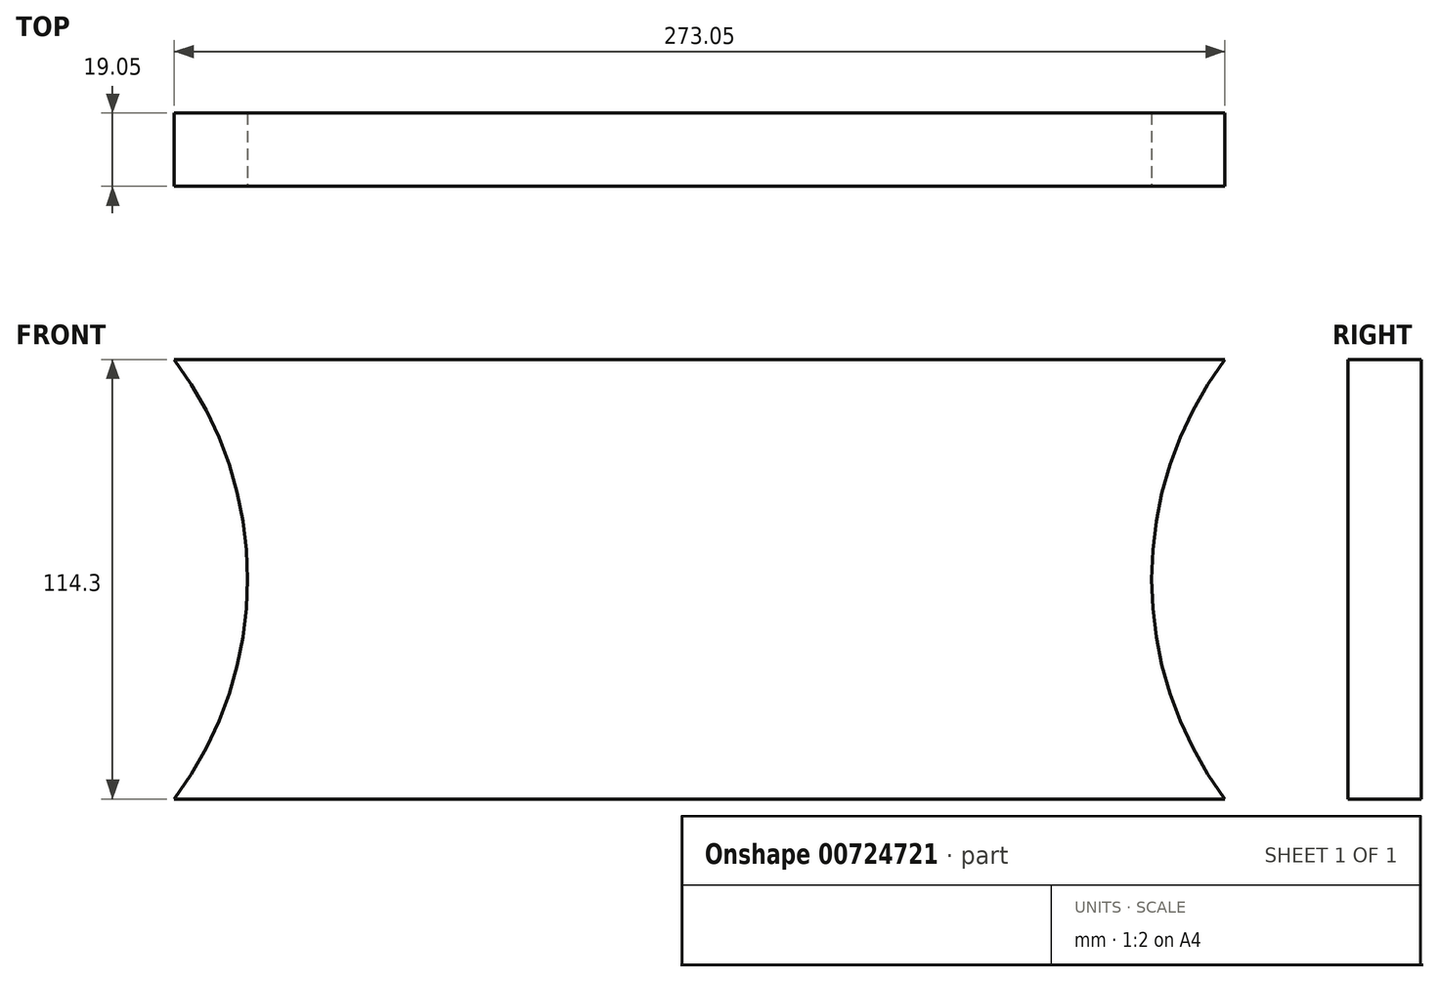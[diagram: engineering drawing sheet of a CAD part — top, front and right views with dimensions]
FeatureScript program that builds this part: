
annotation { "Feature Type Name" : "Feature", "Feature Type Description" : "" }
export const myFeature = defineFeature(function(context is Context, id is Id, definition is map)
    precondition{}
    {
        {
            var Q0;
            Q0=qCreatedBy(makeId("Front.planeOp"),FACE);
            var sketch = newSketch(context, id + "F0", { "sketchPlane" : qUnion([Q0])});
            skLineSegment(sketch, "E0.bottom", {"start": v(0, 0) * mm, "end": v(273.05, 0) * mm});
            skLineSegment(sketch, "E0.top", {"start": v(0, 114.3) * mm, "end": v(273.05, 114.3) * mm});
            skLineSegment(sketch, "E0.left", {"start": v(0, 0) * mm, "end": v(0, 114.3) * mm});
            skLineSegment(sketch, "E0.right", {"start": v(273.05, 0) * mm, "end": v(273.05, 114.3) * mm});
            skSolve(sketch);
        }
        {
            var Q0;
            Q0=qSketchRegion(id+"F0",true);
            extrude(context, id + "F1", {"entities" : qUnion([Q0]), "depth" : 19.05 * mm, "offsetDistance" : 25.4 * mm});
        }
        {
            var Q0;
            Q0=makeQuery(id+"F1.opExtrude","CAP_FACE",FACE,{"disambiguationData":[OSD([sQuery(id+"F0.wireOp",EDGE,"E0.bottom"),sQuery(id+"F0.wireOp",EDGE,"E0.top"),sQuery(id+"F0.wireOp",EDGE,"E0.left"),sQuery(id+"F0.wireOp",EDGE,"E0.right")])],"isStart":false});
            var sketch = newSketch(context, id + "F2", { "sketchPlane" : qUnion([Q0])});
            skArc(sketch, "E1", {"start": v(0, 0) * mm, "mid": v(19.05, 57.15) * mm, "end": v(0, 114.3) * mm});
            skArc(sketch, "E2", {"start": v(273.05, 114.3) * mm, "mid": v(254, 57.15) * mm, "end": v(273.05, 0) * mm});
            skSolve(sketch);
        }
        {
            var Q0;
            Q0=makeQuery(id+"F2.imprint","IMPRINT",FACE,{"disambiguationData":[TD([[makeQuery(id+"F2.imprint","IMPRINT",EDGE,{"derivedFrom":sQuery(id+"F2.wireOp",EDGE,"E1")}),1.0]])]});
            var Q1;
            Q1=makeQuery(id+"F2.imprint","IMPRINT",FACE,{"disambiguationData":[TD([[makeQuery(id+"F2.imprint","IMPRINT",EDGE,{"derivedFrom":sQuery(id+"F2.wireOp",EDGE,"E2")}),1.0]])]});
            extrude(context, id + "F3", {"entities" : qUnion([Q0, Q1]), "operationType" : NewBodyOperationType.REMOVE, "oppositeDirection" : true, "depth" : 25.4 * mm, "offsetDistance" : 25.4 * mm});
        }
    });
